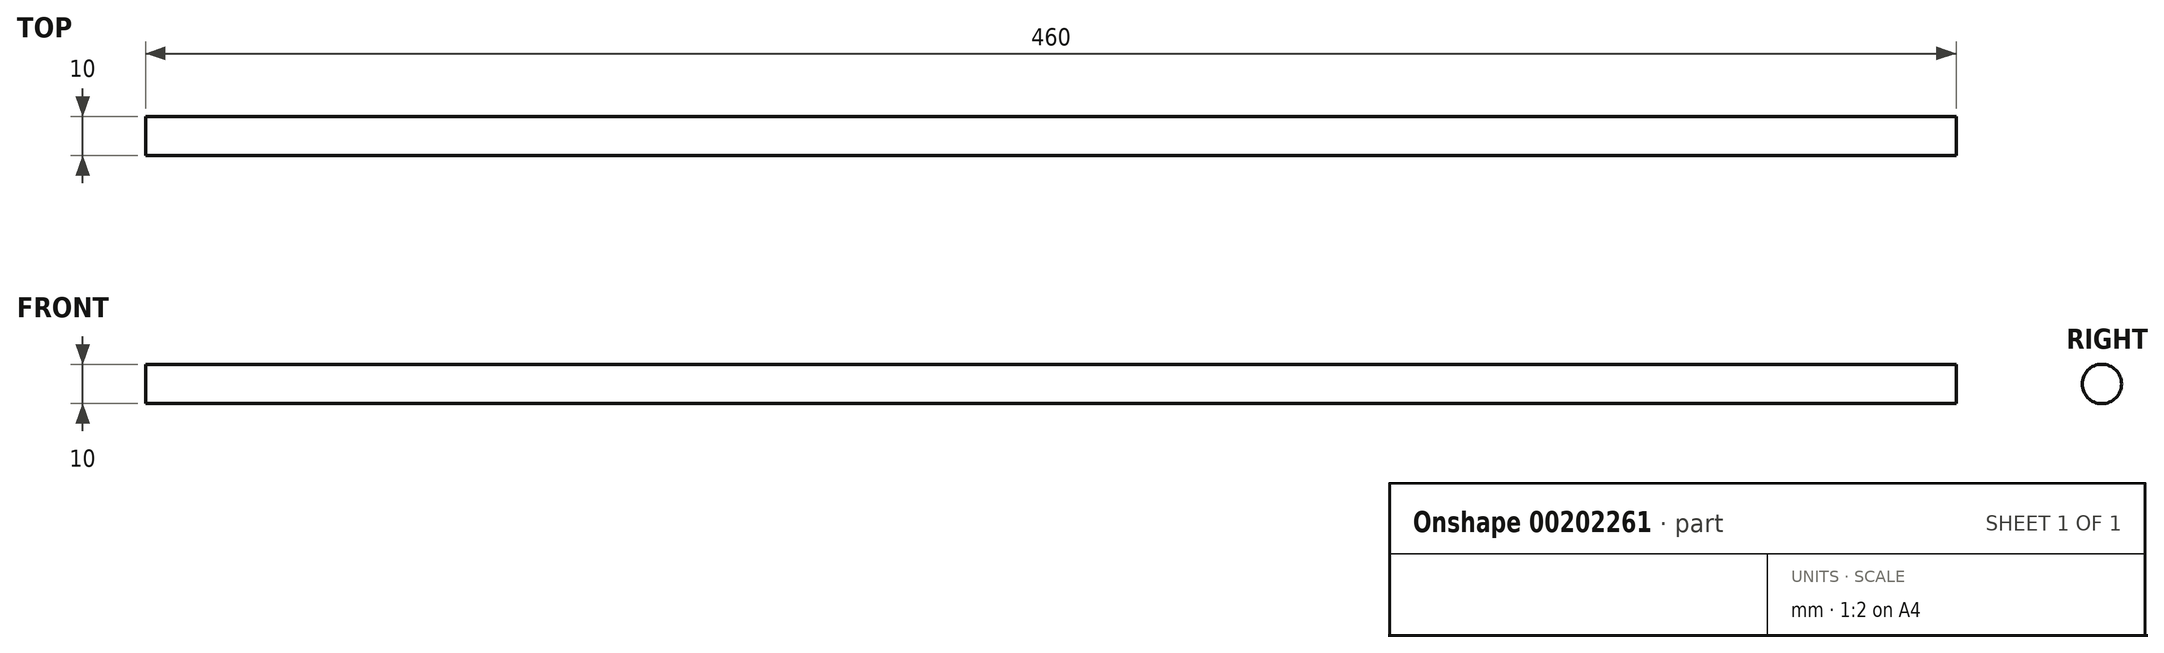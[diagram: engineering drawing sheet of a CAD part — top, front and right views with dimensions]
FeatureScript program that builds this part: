
annotation { "Feature Type Name" : "Feature", "Feature Type Description" : "" }
export const myFeature = defineFeature(function(context is Context, id is Id, definition is map)
    precondition{}
    {
        {
            var Q0;
            Q0=qCreatedBy(makeId("Front.planeOp"),FACE);
            var sketch = newSketch(context, id + "F0", { "sketchPlane" : qUnion([Q0])});
            skLineSegment(sketch, "E0", {"start": v(-138.4, 21.87) * mm, "end": v(321.6, 21.87) * mm});
            skLineSegment(sketch, "E1", {"start": v(-138.4, 26.87) * mm, "end": v(321.6, 26.87) * mm});
            skLineSegment(sketch, "E2", {"start": v(321.6, 21.87) * mm, "end": v(321.6, 26.87) * mm});
            skLineSegment(sketch, "E3", {"start": v(-138.4, 21.87) * mm, "end": v(-138.4, 26.87) * mm});
            skSolve(sketch);
        }
        {
            var Q0;
            Q0=qSketchRegion(id+"F0",true);
            var Q1;
            Q1=sQuery(id+"F0.wireOp",EDGE,"E0");
            revolve(context, id + "F1", {"entities" : qUnion([Q0]), "axis" : qUnion([Q1]), "revolveType" : RevolveType.FULL});
        }
    });
